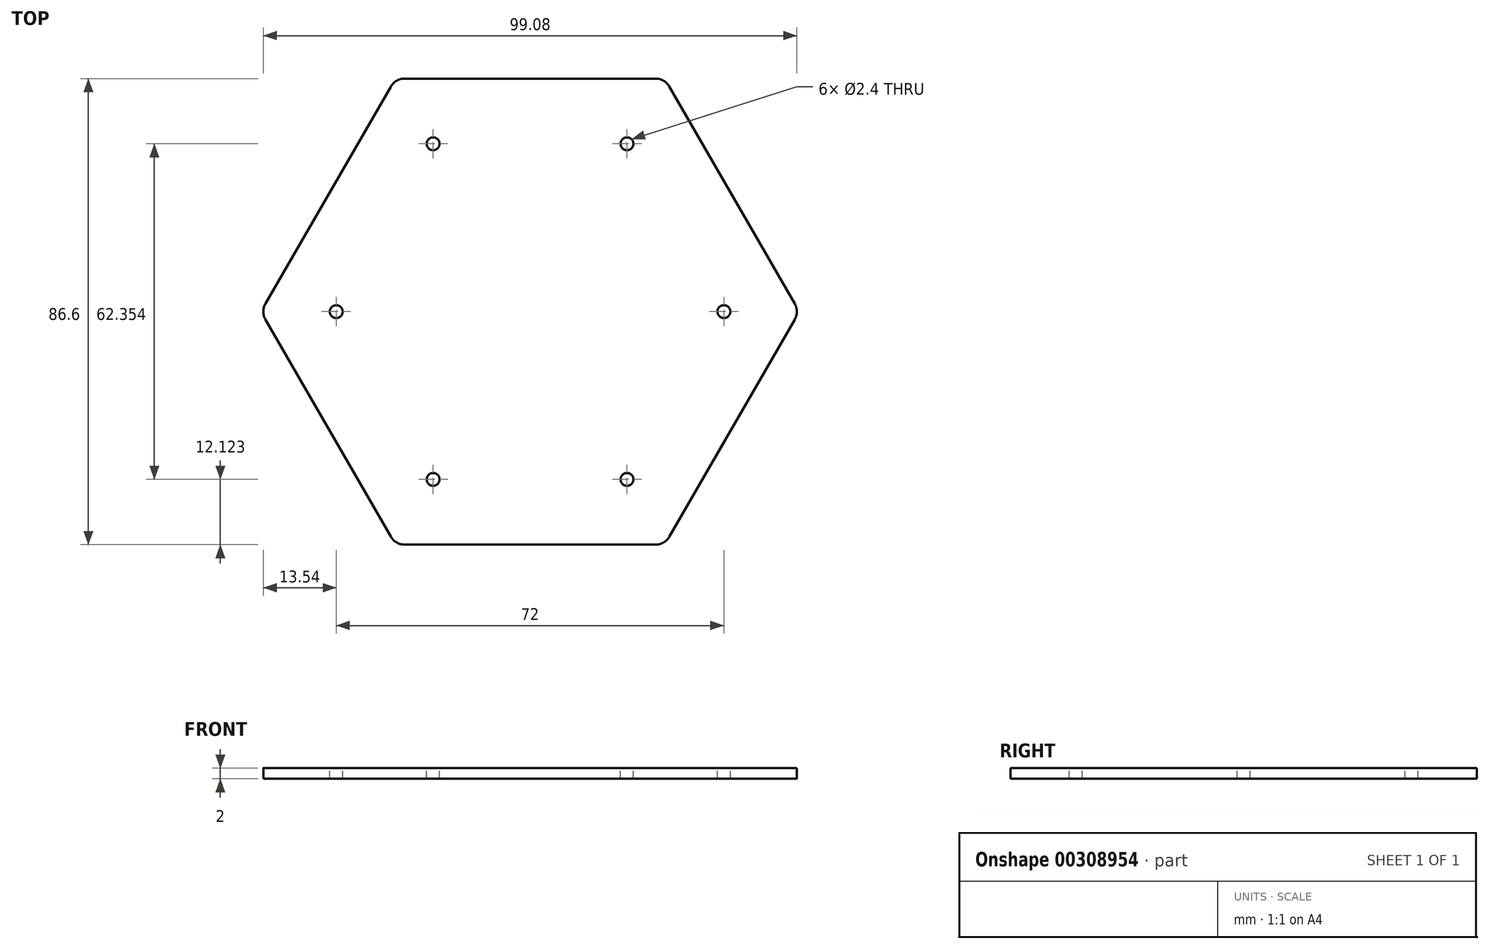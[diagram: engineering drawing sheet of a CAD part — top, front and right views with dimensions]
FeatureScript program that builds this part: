
annotation { "Feature Type Name" : "Feature", "Feature Type Description" : "" }
export const myFeature = defineFeature(function(context is Context, id is Id, definition is map)
    precondition{}
    {
        {
            var Q0;
            Q0=qCreatedBy(makeId("Top.planeOp"),FACE);
            var sketch = newSketch(context, id + "F0", { "sketchPlane" : qUnion([Q0])});
            skCircle(sketch, "E0.cCircle", {"center": v(0, 0) * mm, "radius": 43.3 * mm, "construction": true});
            skLineSegment(sketch, "E0.0", {"start": v(-25, 43.3) * mm, "end": v(25, 43.3) * mm});
            skLineSegment(sketch, "E0.1", {"start": v(25, 43.3) * mm, "end": v(50, 0) * mm});
            skLineSegment(sketch, "E0.2", {"start": v(50, 0) * mm, "end": v(25, -43.3) * mm});
            skLineSegment(sketch, "E0.3", {"start": v(25, -43.3) * mm, "end": v(-25, -43.3) * mm});
            skLineSegment(sketch, "E0.4", {"start": v(-25, -43.3) * mm, "end": v(-50, 0) * mm});
            skLineSegment(sketch, "E0.5", {"start": v(-50, 0) * mm, "end": v(-25, 43.3) * mm});
            skPoint(sketch, "E0.0.midPoint", {"position": v(0, 43.3) * mm});
            skSolve(sketch);
        }
        {
            var Q0;
            Q0 = qSketchRegion(id + "F0", true);
            extrude(context, id + "F1", {"entities" : qUnion([Q0]), "depth" : 2 * mm});
        }
        {
            var Q0;
            Q0=makeQuery(id+"F1.opExtrude","CAP_FACE",FACE,{"disambiguationData":[OSD([sQuery(id+"F0.wireOp",EDGE,"E0.0"),sQuery(id+"F0.wireOp",EDGE,"E0.1"),sQuery(id+"F0.wireOp",EDGE,"E0.2"),sQuery(id+"F0.wireOp",EDGE,"E0.3"),sQuery(id+"F0.wireOp",EDGE,"E0.4"),sQuery(id+"F0.wireOp",EDGE,"E0.5")])],"isStart":false});
            var sketch = newSketch(context, id + "F2", { "sketchPlane" : qUnion([Q0])});
            skCircle(sketch, "E1.cCircle", {"center": v(0, 0) * mm, "radius": 31.18 * mm, "construction": true});
            skLineSegment(sketch, "E1.0", {"start": v(-18, 31.18) * mm, "end": v(18, 31.18) * mm});
            skLineSegment(sketch, "E1.1", {"start": v(18, 31.18) * mm, "end": v(36, 0) * mm});
            skLineSegment(sketch, "E1.2", {"start": v(36, 0) * mm, "end": v(18, -31.18) * mm});
            skLineSegment(sketch, "E1.3", {"start": v(18, -31.18) * mm, "end": v(-18, -31.18) * mm});
            skLineSegment(sketch, "E1.4", {"start": v(-18, -31.18) * mm, "end": v(-36, 0) * mm});
            skLineSegment(sketch, "E1.5", {"start": v(-36, 0) * mm, "end": v(-18, 31.18) * mm});
            skPoint(sketch, "E1.0.midPoint", {"position": v(0, 31.18) * mm});
            skSolve(sketch);
        }
        {
            var Q0;
            Q0=sQuery(id+"F2.wireOp",VERTEX,"E1.0.start");
            var Q1;
            Q1=sQuery(id+"F2.wireOp",VERTEX,"E1.1.start");
            var Q2;
            Q2=sQuery(id+"F2.wireOp",VERTEX,"E1.2.start");
            var Q3;
            Q3=sQuery(id+"F2.wireOp",VERTEX,"E1.3.start");
            var Q4;
            Q4=sQuery(id+"F2.wireOp",VERTEX,"E1.4.start");
            var Q5;
            Q5=sQuery(id+"F2.wireOp",VERTEX,"E1.5.start");
            var Q6;
            Q6=makeQuery(id+"F1.opExtrude","SWEPT_BODY",BODY,{"disambiguationData":[OSD([sQuery(id+"F0.wireOp",EDGE,"E0.0"),sQuery(id+"F0.wireOp",EDGE,"E0.1"),sQuery(id+"F0.wireOp",EDGE,"E0.2"),sQuery(id+"F0.wireOp",EDGE,"E0.3"),sQuery(id+"F0.wireOp",EDGE,"E0.4"),sQuery(id+"F0.wireOp",EDGE,"E0.5")])]});
            hole(context, id + "F3", {"style" : HoleStyle.SIMPLE, "endStyle" : HoleEndStyle.THROUGH, "standardTappedOrClearance" : lookupTablePath({ "standard" : "ISO", "engagement" : "75%", "pitch" : "0.6 mm", "size" : "M3", "type" : "Tapped" }), "standardBlindInLast" : lookupTablePath({ "standard" : "ISO", "engagement" : "75%", "pitch" : "0.6 mm", "size" : "M3", "type" : "Tapped" }), "holeDiameter" : 2.4 * mm, "showTappedDepth" : true, "tappedDepth" : 12 * mm, "tapClearance" : 3, "locations" : qUnion([Q0, Q1, Q2, Q3, Q4, Q5]), "scope" : qUnion([Q6])});
        }
        {
            var Q0;
            Q0=makeQuery(id+"F1.opExtrude","SWEPT_EDGE",EDGE,{"disambiguationData":[OSD([sQuery(id+"F0.wireOp",EDGE,"E0.3"),sQuery(id+"F0.wireOp",EDGE,"E0.4")])]});
            var Q1;
            Q1=makeQuery(id+"F1.opExtrude","SWEPT_EDGE",EDGE,{"disambiguationData":[OSD([sQuery(id+"F0.wireOp",EDGE,"E0.2"),sQuery(id+"F0.wireOp",EDGE,"E0.3")])]});
            var Q2;
            Q2=makeQuery(id+"F1.opExtrude","SWEPT_EDGE",EDGE,{"disambiguationData":[OSD([sQuery(id+"F0.wireOp",EDGE,"E0.1"),sQuery(id+"F0.wireOp",EDGE,"E0.2")])]});
            var Q3;
            Q3=makeQuery(id+"F1.opExtrude","SWEPT_EDGE",EDGE,{"disambiguationData":[OSD([sQuery(id+"F0.wireOp",EDGE,"E0.0"),sQuery(id+"F0.wireOp",EDGE,"E0.1")])]});
            var Q4;
            Q4=makeQuery(id+"F1.opExtrude","SWEPT_EDGE",EDGE,{"disambiguationData":[OSD([sQuery(id+"F0.wireOp",EDGE,"E0.0"),sQuery(id+"F0.wireOp",EDGE,"E0.5")])]});
            var Q5;
            Q5=makeQuery(id+"F1.opExtrude","SWEPT_EDGE",EDGE,{"disambiguationData":[OSD([sQuery(id+"F0.wireOp",EDGE,"E0.4"),sQuery(id+"F0.wireOp",EDGE,"E0.5")])]});
            fillet(context, id + "F4", {"entities" : qUnion([Q0, Q1, Q2, Q3, Q4, Q5]), "radius" : 3 * mm, "tangentPropagation" : true, "allowEdgeOverflow" : false});
        }
    });
